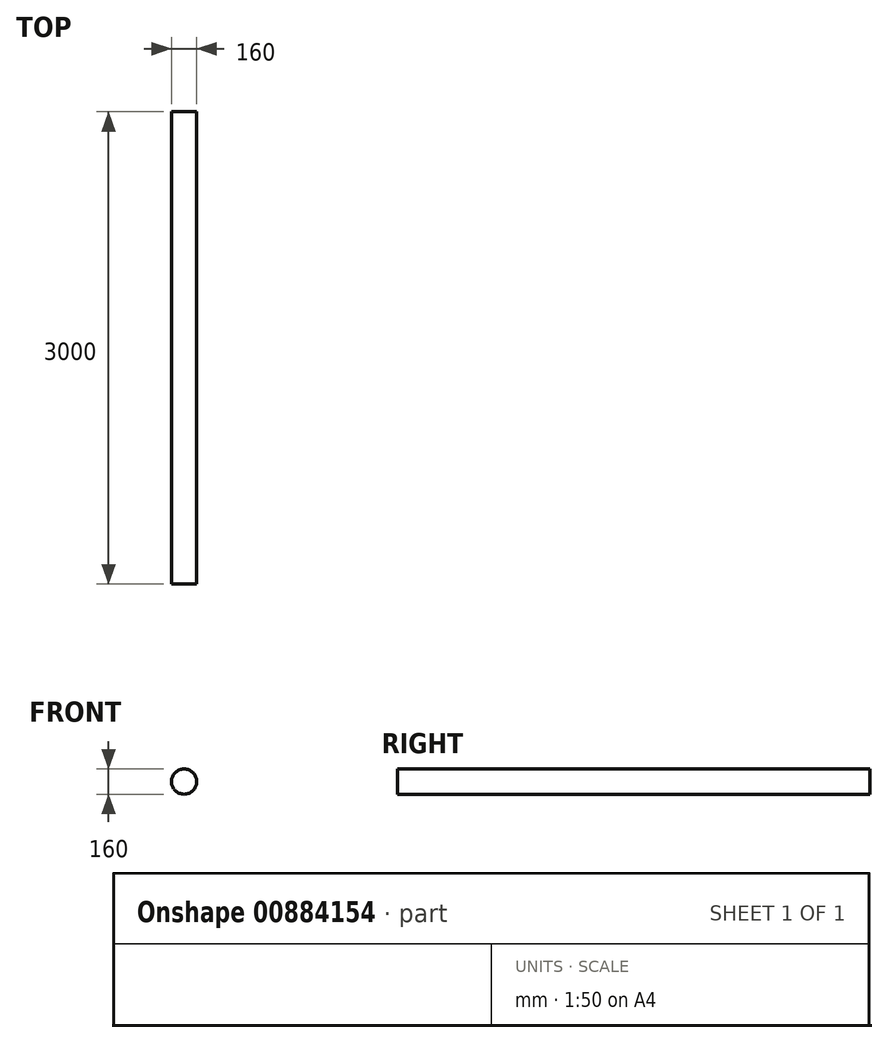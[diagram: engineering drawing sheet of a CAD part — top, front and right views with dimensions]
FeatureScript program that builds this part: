
annotation { "Feature Type Name" : "Feature", "Feature Type Description" : "" }
export const myFeature = defineFeature(function(context is Context, id is Id, definition is map)
    precondition{}
    {
        {
            var Q0;
            Q0=qCreatedBy(makeId("Front.planeOp"),FACE);
            var sketch = newSketch(context, id + "F0", { "sketchPlane" : qUnion([Q0])});
            skCircle(sketch, "E0", {"center": v(0, 0) * mm, "radius": 80 * mm});
            skSolve(sketch);
        }
        {
            var Q0;
            Q0=makeQuery(id+"F0.imprint","IMPRINT",FACE,{"disambiguationData":[TD([[makeQuery(id+"F0.imprint","IMPRINT",EDGE,{"derivedFrom":sQuery(id+"F0.wireOp",EDGE,"E0")}),1.0]])]});
            extrude(context, id + "F1", {"entities" : qUnion([Q0]), "depth" : 3000 * mm, "offsetDistance" : 25 * mm});
        }
    });
